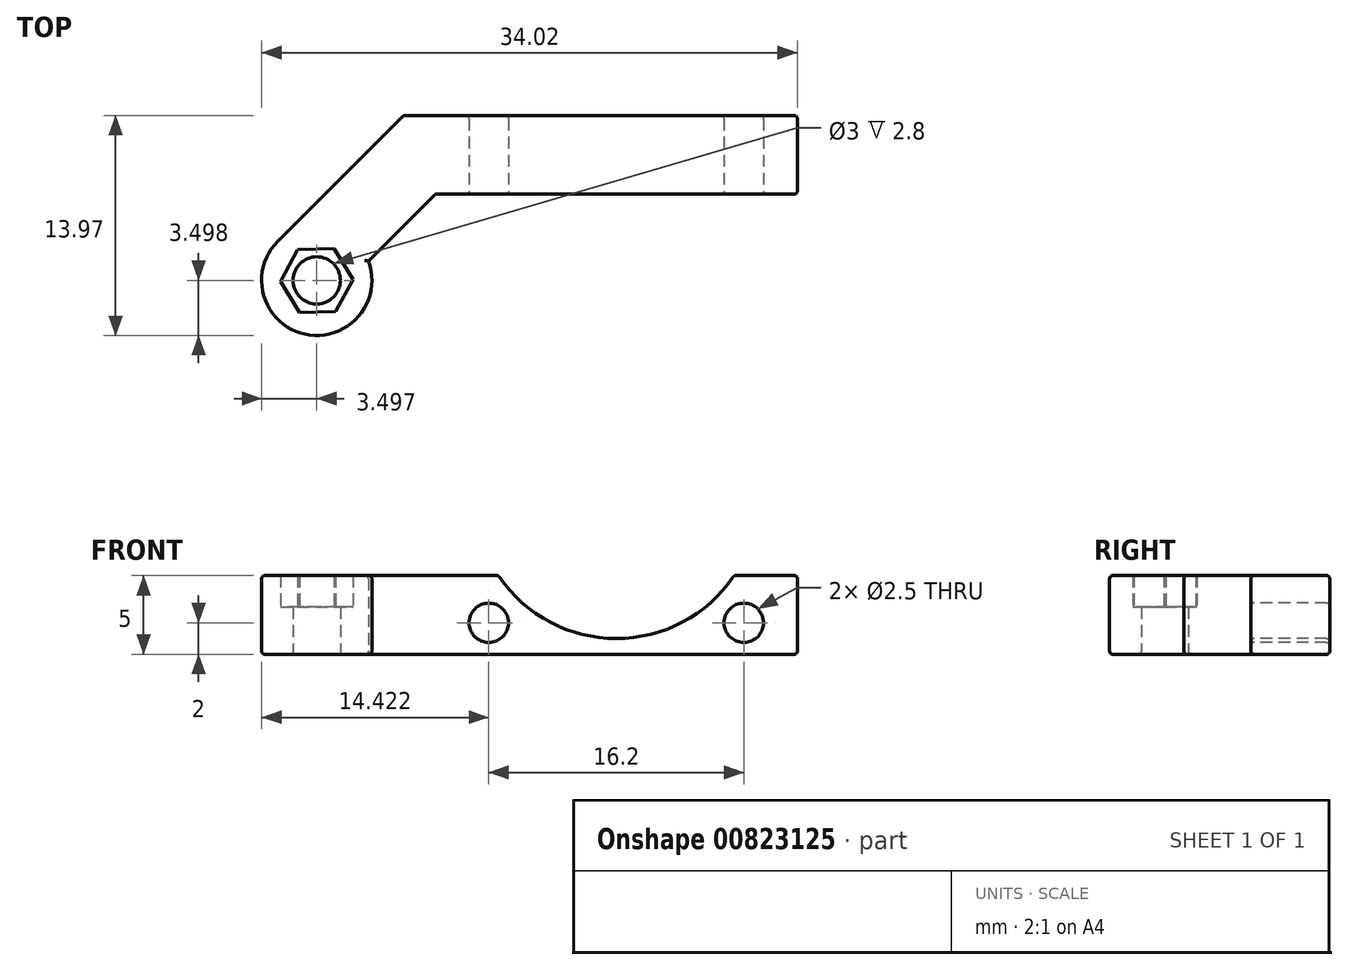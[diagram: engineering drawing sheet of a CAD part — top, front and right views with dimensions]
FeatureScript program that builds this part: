
annotation { "Feature Type Name" : "Feature", "Feature Type Description" : "" }
export const myFeature = defineFeature(function(context is Context, id is Id, definition is map)
    precondition{}
    {
        {
            var Q0;
            Q0=qCreatedBy(makeId("Top.planeOp"),FACE);
            var sketch = newSketch(context, id + "F0", { "sketchPlane" : qUnion([Q0])});
            skLineSegment(sketch, "E0", {"start": v(22.84, 7.04) * mm, "end": v(-2.16, 7.04) * mm});
            skLineSegment(sketch, "E1", {"start": v(-0.16, 2.04) * mm, "end": v(22.84, 2.04) * mm});
            skLineSegment(sketch, "E2", {"start": v(22.84, 2.04) * mm, "end": v(22.84, 7.04) * mm});
            skCircle(sketch, "E3", {"center": v(-7.68, -3.43) * mm, "radius": 1.5 * mm});
            skLineSegment(sketch, "E4", {"start": v(-7.68, 0) * mm, "end": v(-7.68, -6.73) * mm, "construction": true});
            skCircle(sketch, "E5", {"center": v(-7.68, -3.43) * mm, "radius": 3.5 * mm});
            skLineSegment(sketch, "E6", {"start": v(-2.16, 7.04) * mm, "end": v(-10.16, -0.96) * mm});
            skLineSegment(sketch, "E7", {"start": v(-4.4, -2.2) * mm, "end": v(-0.16, 2.04) * mm});
            skCircle(sketch, "E8.cCircle", {"center": v(-7.68, -3.43) * mm, "radius": 2 * mm, "construction": true});
            skLineSegment(sketch, "E8.0", {"start": v(-5.37, -3.37) * mm, "end": v(-6.47, -5.4) * mm});
            skLineSegment(sketch, "E8.1", {"start": v(-6.47, -5.4) * mm, "end": v(-8.78, -5.46) * mm});
            skLineSegment(sketch, "E8.2", {"start": v(-8.78, -5.46) * mm, "end": v(-10, -3.5) * mm});
            skLineSegment(sketch, "E8.3", {"start": v(-10, -3.5) * mm, "end": v(-8.9, -1.47) * mm});
            skLineSegment(sketch, "E8.4", {"start": v(-8.9, -1.47) * mm, "end": v(-6.59, -1.4) * mm});
            skLineSegment(sketch, "E8.5", {"start": v(-6.59, -1.4) * mm, "end": v(-5.37, -3.37) * mm});
            skPoint(sketch, "E8.0.midPoint", {"position": v(-5.92, -4.38) * mm});
            skSolve(sketch);
        }
        {
            var Q0;
            Q0 = qSketchRegion(id + "F0", true);
            var Q1;
            Q1=makeQuery(id+"F0.imprint","IMPRINT",FACE,{"disambiguationData":[TD([[makeQuery(id+"F0.imprint","IMPRINT",EDGE,{"derivedFrom":sQuery(id+"F0.wireOp",EDGE,"E3")}),-1.0]])]});
            extrude(context, id + "F1", {"entities" : qUnion([Q0, Q1]), "depth" : 5 * mm, "offsetDistance" : 25 * mm});
        }
        {
            var Q0;
            Q0=qCreatedBy(makeId("Front.planeOp"),FACE);
            var sketch = newSketch(context, id + "F2", { "sketchPlane" : qUnion([Q0])});
            skLineSegment(sketch, "E9", {"start": v(46.77, 2.5) * mm, "end": v(-32, 2.5) * mm, "construction": true});
            skLineSegment(sketch, "E10", {"start": v(11.34, 15) * mm, "end": v(11.34, 0) * mm, "construction": true});
            skCircle(sketch, "E11", {"center": v(3.24, 2) * mm, "radius": 1.25 * mm});
            skCircle(sketch, "E12", {"center": v(19.44, 2) * mm, "radius": 1.25 * mm});
            skCircle(sketch, "E13", {"center": v(11.34, 10) * mm, "radius": 9 * mm});
            skSolve(sketch);
        }
        {
            var Q0;
            Q0=makeQuery(id+"F2.imprint","IMPRINT",FACE,{"disambiguationData":[TD([[makeQuery(id+"F2.imprint","IMPRINT",EDGE,{"derivedFrom":sQuery(id+"F2.wireOp",EDGE,"E13")}),1.0]])]});
            var Q1;
            Q1=makeQuery(id+"F2.imprint","IMPRINT",FACE,{"disambiguationData":[TD([[makeQuery(id+"F2.imprint","IMPRINT",EDGE,{"derivedFrom":sQuery(id+"F2.wireOp",EDGE,"E12")}),1.0]])]});
            var Q2;
            Q2=makeQuery(id+"F2.imprint","IMPRINT",FACE,{"disambiguationData":[TD([[makeQuery(id+"F2.imprint","IMPRINT",EDGE,{"derivedFrom":sQuery(id+"F2.wireOp",EDGE,"E11")}),1.0]])]});
            var Q3;
            Q3=sQuery(id+"F2.wireOp",EDGE,"E13");
            var Q4;
            Q4=sQuery(id+"F2.wireOp",EDGE,"E12");
            var Q5;
            Q5=sQuery(id+"F2.wireOp",EDGE,"E11");
            extrude(context, id + "F3", {"entities" : qUnion([Q0, Q1, Q2]), "operationType" : NewBodyOperationType.REMOVE, "surfaceEntities" : qUnion([Q3, Q4, Q5]), "depth" : -15 * mm, "offsetDistance" : 25 * mm});
        }
        {
            var Q0;
            {var subQ0=sQuery(id+"F0.wireOp",EDGE,"E0");var subQ1=sQuery(id+"F0.wireOp",EDGE,"E2");Q0=makeQuery(id+"F3.boolean.opBoolean","SPLIT",EDGE,{"disambiguationData":[TD([makeQuery(id+"F1.opExtrude","SWEPT_FACE",FACE,{"disambiguationData":[OSD([subQ1])]})])],"derivedFrom":makeQuery(id+"F1.opExtrude","CAP_EDGE",EDGE,{"disambiguationData":[OSD([subQ0])],"isStart":false})});}
            var Q1;
            Q1=makeQuery(id+"F3.boolean.opBoolean","INTERSECT",EDGE,{"derivedFrom":[makeQuery(id+"F1.opExtrude","SWEPT_FACE",FACE,{"disambiguationData":[OSD([sQuery(id+"F0.wireOp",EDGE,"E0")])]}),makeQuery(id+"F3.opExtrude","SWEPT_FACE",FACE,{"disambiguationData":[OSD([sQuery(id+"F2.wireOp",EDGE,"E13")])]})]});
            var Q2;
            Q2=makeQuery(id+"F1.opExtrude","SWEPT_FACE",FACE,{"disambiguationData":[OSD([sQuery(id+"F0.wireOp",EDGE,"E1")])]});
            var Q3;
            Q3=makeQuery(id+"F1.opExtrude","SWEPT_FACE",FACE,{"disambiguationData":[OSD([sQuery(id+"F0.wireOp",EDGE,"E3")])]});
            var Q4;
            Q4=makeQuery(id+"F1.opExtrude","CAP_EDGE",EDGE,{"disambiguationData":[OSD([sQuery(id+"F0.wireOp",EDGE,"E2")])],"isStart":false});
            var Q5;
            Q5=makeQuery(id+"F1.opExtrude","CAP_EDGE",EDGE,{"disambiguationData":[OSD([sQuery(id+"F0.wireOp",EDGE,"0f24549b-c2e2-4721-b6e2-35617bd255be")])],"isStart":true});
            var Q6;
            Q6=makeQuery(id+"F1.opExtrude","SWEPT_EDGE",EDGE,{"disambiguationData":[OSD([sQuery(id+"F0.wireOp",EDGE,"Zt6ANnRh-k5cY-9Nom-YIyw-pIJQE4WEo30R"),sQuery(id+"F0.wireOp",EDGE,"0tKCsk9C-eRW9-mIZ1-Uz5l-tO1zgxtLd7ai")])]});
            var Q7;
            {var subQ0=sQuery(id+"F0.wireOp",EDGE,"E2");var subQ1=sQuery(id+"F0.wireOp",EDGE,"E1");Q7=makeQuery(id+"F3.boolean.opBoolean","SPLIT",EDGE,{"disambiguationData":[TD([makeQuery(id+"F1.opExtrude","SWEPT_FACE",FACE,{"disambiguationData":[OSD([subQ0])]})])],"derivedFrom":makeQuery(id+"F1.opExtrude","CAP_EDGE",EDGE,{"disambiguationData":[OSD([subQ1])],"isStart":false})});}
            var Q8;
            {var subQ0=sQuery(id+"F0.wireOp",EDGE,"E0");var subQ1=sQuery(id+"F0.wireOp",EDGE,"XOKBXjMK-aIrR-3Xav-z1c1-2tbnTsD4K69U");Q8=makeQuery(id+"F3.boolean.opBoolean","SPLIT",EDGE,{"disambiguationData":[TD([makeQuery(id+"F1.opExtrude","SWEPT_FACE",FACE,{"disambiguationData":[OSD([subQ1])]})])],"derivedFrom":makeQuery(id+"F1.opExtrude","CAP_EDGE",EDGE,{"disambiguationData":[OSD([subQ0])],"isStart":false})});}
            var Q9;
            Q9=makeQuery(id+"F3.boolean.opBoolean","INTERSECT",EDGE,{"disambiguationData":[OD(0.0)],"derivedFrom":[makeQuery(id+"F1.opExtrude","CAP_FACE",FACE,{"disambiguationData":[OSD([sQuery(id+"F0.wireOp",EDGE,"E0"),sQuery(id+"F0.wireOp",EDGE,"XOKBXjMK-aIrR-3Xav-z1c1-2tbnTsD4K69U"),sQuery(id+"F0.wireOp",EDGE,"5qDD20kP-8p41-NuGR-BYb0-utjdQ8Pf2vNB"),sQuery(id+"F0.wireOp",EDGE,"Zt6ANnRh-k5cY-9Nom-YIyw-pIJQE4WEo30R"),sQuery(id+"F0.wireOp",EDGE,"0tKCsk9C-eRW9-mIZ1-Uz5l-tO1zgxtLd7ai"),sQuery(id+"F0.wireOp",EDGE,"E1"),sQuery(id+"F0.wireOp",EDGE,"E2"),sQuery(id+"F0.wireOp",EDGE,"0f24549b-c2e2-4721-b6e2-35617bd255be"),sQuery(id+"F0.wireOp",EDGE,"E3")])],"isStart":false}),makeQuery(id+"F3.opExtrude","SWEPT_FACE",FACE,{"disambiguationData":[OSD([sQuery(id+"F2.wireOp",EDGE,"E13")])]})]});
            var Q10;
            {var subQ0=sQuery(id+"F0.wireOp",EDGE,"E1");var subQ1=sQuery(id+"F0.wireOp",EDGE,"0tKCsk9C-eRW9-mIZ1-Uz5l-tO1zgxtLd7ai");Q10=makeQuery(id+"F3.boolean.opBoolean","SPLIT",EDGE,{"disambiguationData":[TD([makeQuery(id+"F1.opExtrude","SWEPT_FACE",FACE,{"disambiguationData":[OSD([subQ1])]})])],"derivedFrom":makeQuery(id+"F1.opExtrude","CAP_EDGE",EDGE,{"disambiguationData":[OSD([subQ0])],"isStart":false})});}
            var Q11;
            Q11=makeQuery(id+"F1.opExtrude","CAP_EDGE",EDGE,{"disambiguationData":[OSD([sQuery(id+"F0.wireOp",EDGE,"Zt6ANnRh-k5cY-9Nom-YIyw-pIJQE4WEo30R")])],"isStart":false});
            var Q12;
            Q12=makeQuery(id+"F3.boolean.opBoolean","INTERSECT",EDGE,{"derivedFrom":[makeQuery(id+"F1.opExtrude","SWEPT_FACE",FACE,{"disambiguationData":[OSD([sQuery(id+"F0.wireOp",EDGE,"E1")])]}),makeQuery(id+"F3.opExtrude","SWEPT_FACE",FACE,{"disambiguationData":[OSD([sQuery(id+"F2.wireOp",EDGE,"E11")])]})]});
            var Q13;
            Q13=makeQuery(id+"F1.opExtrude","CAP_EDGE",EDGE,{"disambiguationData":[OSD([sQuery(id+"F0.wireOp",EDGE,"E2")])],"isStart":true});
            var Q14;
            Q14=makeQuery(id+"F1.opExtrude","CAP_FACE",FACE,{"disambiguationData":[OSD([sQuery(id+"F0.wireOp",EDGE,"E0"),sQuery(id+"F0.wireOp",EDGE,"XOKBXjMK-aIrR-3Xav-z1c1-2tbnTsD4K69U"),sQuery(id+"F0.wireOp",EDGE,"5qDD20kP-8p41-NuGR-BYb0-utjdQ8Pf2vNB"),sQuery(id+"F0.wireOp",EDGE,"Zt6ANnRh-k5cY-9Nom-YIyw-pIJQE4WEo30R"),sQuery(id+"F0.wireOp",EDGE,"0tKCsk9C-eRW9-mIZ1-Uz5l-tO1zgxtLd7ai"),sQuery(id+"F0.wireOp",EDGE,"E1"),sQuery(id+"F0.wireOp",EDGE,"E2"),sQuery(id+"F0.wireOp",EDGE,"0f24549b-c2e2-4721-b6e2-35617bd255be"),sQuery(id+"F0.wireOp",EDGE,"E3")])],"isStart":true});
            var Q15;
            Q15=makeQuery(id+"F1.opExtrude","CAP_EDGE",EDGE,{"disambiguationData":[OSD([sQuery(id+"F0.wireOp",EDGE,"XOKBXjMK-aIrR-3Xav-z1c1-2tbnTsD4K69U")])],"isStart":false});
            var Q16;
            Q16=makeQuery(id+"F1.opExtrude","CAP_EDGE",EDGE,{"disambiguationData":[OSD([sQuery(id+"F0.wireOp",EDGE,"0tKCsk9C-eRW9-mIZ1-Uz5l-tO1zgxtLd7ai")])],"isStart":false});
            var Q17;
            {var subQ0=sQuery(id+"F0.wireOp",EDGE,"5qDD20kP-8p41-NuGR-BYb0-utjdQ8Pf2vNB");var subQ1=sQuery(id+"F0.wireOp",EDGE,"XOKBXjMK-aIrR-3Xav-z1c1-2tbnTsD4K69U");var subQ2=sQuery(id+"F0.wireOp",EDGE,"Zt6ANnRh-k5cY-9Nom-YIyw-pIJQE4WEo30R");var subQ3=sQuery(id+"F0.wireOp",EDGE,"E0");var subQ4=sQuery(id+"F0.wireOp",EDGE,"0tKCsk9C-eRW9-mIZ1-Uz5l-tO1zgxtLd7ai");var subQ5=sQuery(id+"F0.wireOp",EDGE,"E1");var subQ6=sQuery(id+"F0.wireOp",EDGE,"0f24549b-c2e2-4721-b6e2-35617bd255be");var subQ7=sQuery(id+"F0.wireOp",EDGE,"E3");Q17=makeQuery(id+"F3.boolean.opBoolean","SPLIT",FACE,{"disambiguationData":[TD([makeQuery(id+"F1.opExtrude","SWEPT_FACE",FACE,{"disambiguationData":[OSD([subQ1])]})])],"derivedFrom":makeQuery(id+"F1.opExtrude","CAP_FACE",FACE,{"disambiguationData":[OSD([subQ3,subQ1,subQ0,subQ2,subQ4,subQ5,sQuery(id+"F0.wireOp",EDGE,"E2"),subQ6,subQ7])],"isStart":false})});}
            var Q18;
            Q18=makeQuery(id+"F1.opExtrude","SWEPT_EDGE",EDGE,{"disambiguationData":[OSD([sQuery(id+"F0.wireOp",EDGE,"E1"),sQuery(id+"F0.wireOp",EDGE,"E2")])]});
            var Q19;
            Q19=makeQuery(id+"F1.opExtrude","SWEPT_EDGE",EDGE,{"disambiguationData":[OSD([sQuery(id+"F0.wireOp",EDGE,"0tKCsk9C-eRW9-mIZ1-Uz5l-tO1zgxtLd7ai"),sQuery(id+"F0.wireOp",EDGE,"E1")])]});
            var Q20;
            Q20=makeQuery(id+"F1.opExtrude","CAP_EDGE",EDGE,{"disambiguationData":[OSD([sQuery(id+"F0.wireOp",EDGE,"E1")])],"isStart":true});
            var Q21;
            Q21=makeQuery(id+"F3.boolean.opBoolean","COPY",FACE,{"derivedFrom":makeQuery(id+"F3.opExtrude","SWEPT_FACE",FACE,{"disambiguationData":[OSD([sQuery(id+"F2.wireOp",EDGE,"E12")])]})});
            var Q22;
            Q22=makeQuery(id+"F1.opExtrude","CAP_EDGE",EDGE,{"disambiguationData":[OSD([sQuery(id+"F0.wireOp",EDGE,"Zt6ANnRh-k5cY-9Nom-YIyw-pIJQE4WEo30R")])],"isStart":true});
            var Q23;
            Q23=makeQuery(id+"F1.opExtrude","CAP_EDGE",EDGE,{"disambiguationData":[OSD([sQuery(id+"F0.wireOp",EDGE,"0f24549b-c2e2-4721-b6e2-35617bd255be")])],"isStart":false});
            var Q24;
            {var subQ0=sQuery(id+"F0.wireOp",EDGE,"E0");var subQ1=sQuery(id+"F0.wireOp",EDGE,"E1");var subQ2=sQuery(id+"F0.wireOp",EDGE,"E2");Q24=makeQuery(id+"F3.boolean.opBoolean","SPLIT",FACE,{"disambiguationData":[TD([makeQuery(id+"F1.opExtrude","SWEPT_FACE",FACE,{"disambiguationData":[OSD([subQ2])]})])],"derivedFrom":makeQuery(id+"F1.opExtrude","CAP_FACE",FACE,{"disambiguationData":[OSD([subQ0,sQuery(id+"F0.wireOp",EDGE,"XOKBXjMK-aIrR-3Xav-z1c1-2tbnTsD4K69U"),sQuery(id+"F0.wireOp",EDGE,"5qDD20kP-8p41-NuGR-BYb0-utjdQ8Pf2vNB"),sQuery(id+"F0.wireOp",EDGE,"Zt6ANnRh-k5cY-9Nom-YIyw-pIJQE4WEo30R"),sQuery(id+"F0.wireOp",EDGE,"0tKCsk9C-eRW9-mIZ1-Uz5l-tO1zgxtLd7ai"),subQ1,subQ2,sQuery(id+"F0.wireOp",EDGE,"0f24549b-c2e2-4721-b6e2-35617bd255be"),sQuery(id+"F0.wireOp",EDGE,"E3")])],"isStart":false})});}
            var Q25;
            Q25=makeQuery(id+"F1.opExtrude","SWEPT_FACE",FACE,{"disambiguationData":[OSD([sQuery(id+"F0.wireOp",EDGE,"XOKBXjMK-aIrR-3Xav-z1c1-2tbnTsD4K69U")])]});
            var Q26;
            Q26=makeQuery(id+"F1.opExtrude","CAP_EDGE",EDGE,{"disambiguationData":[OSD([sQuery(id+"F0.wireOp",EDGE,"0tKCsk9C-eRW9-mIZ1-Uz5l-tO1zgxtLd7ai")])],"isStart":true});
            var Q27;
            Q27=makeQuery(id+"F1.opExtrude","SWEPT_FACE",FACE,{"disambiguationData":[OSD([sQuery(id+"F0.wireOp",EDGE,"E2")])]});
            var Q28;
            Q28=makeQuery(id+"F1.opExtrude","SWEPT_FACE",FACE,{"disambiguationData":[OSD([sQuery(id+"F0.wireOp",EDGE,"5qDD20kP-8p41-NuGR-BYb0-utjdQ8Pf2vNB")])]});
            var Q29;
            Q29=makeQuery(id+"F3.boolean.opBoolean","COPY",FACE,{"derivedFrom":makeQuery(id+"F3.opExtrude","SWEPT_FACE",FACE,{"disambiguationData":[OSD([sQuery(id+"F2.wireOp",EDGE,"E13")])]})});
            var Q30;
            Q30=makeQuery(id+"F3.boolean.opBoolean","INTERSECT",EDGE,{"derivedFrom":[makeQuery(id+"F1.opExtrude","SWEPT_FACE",FACE,{"disambiguationData":[OSD([sQuery(id+"F0.wireOp",EDGE,"E1")])]}),makeQuery(id+"F3.opExtrude","SWEPT_FACE",FACE,{"disambiguationData":[OSD([sQuery(id+"F2.wireOp",EDGE,"E12")])]})]});
            var Q31;
            Q31=makeQuery(id+"F3.boolean.opBoolean","INTERSECT",EDGE,{"derivedFrom":[makeQuery(id+"F1.opExtrude","SWEPT_FACE",FACE,{"disambiguationData":[OSD([sQuery(id+"F0.wireOp",EDGE,"E1")])]}),makeQuery(id+"F3.opExtrude","SWEPT_FACE",FACE,{"disambiguationData":[OSD([sQuery(id+"F2.wireOp",EDGE,"E13")])]})]});
            var Q32;
            Q32=makeQuery(id+"F1.opExtrude","SWEPT_EDGE",EDGE,{"disambiguationData":[OSD([sQuery(id+"F0.wireOp",EDGE,"E0"),sQuery(id+"F0.wireOp",EDGE,"E2")])]});
            var Q33;
            Q33=makeQuery(id+"F1.opExtrude","SWEPT_EDGE",EDGE,{"disambiguationData":[OSD([sQuery(id+"F0.wireOp",EDGE,"l5DqmruQ-S4Sb-Dlvx-ZIcM-rorxe7HzB1pB"),sQuery(id+"F0.wireOp",EDGE,"Zt6ANnRh-k5cY-9Nom-YIyw-pIJQE4WEo30R"),sQuery(id+"F0.wireOp",EDGE,"0f24549b-c2e2-4721-b6e2-35617bd255be")])]});
            var Q34;
            Q34=makeQuery(id+"F1.opExtrude","SWEPT_FACE",FACE,{"disambiguationData":[OSD([sQuery(id+"F0.wireOp",EDGE,"E0")])]});
            var Q35;
            Q35=makeQuery(id+"F1.opExtrude","SWEPT_FACE",FACE,{"disambiguationData":[OSD([sQuery(id+"F0.wireOp",EDGE,"0tKCsk9C-eRW9-mIZ1-Uz5l-tO1zgxtLd7ai")])]});
            var Q36;
            Q36=makeQuery(id+"F1.opExtrude","CAP_EDGE",EDGE,{"disambiguationData":[OSD([sQuery(id+"F0.wireOp",EDGE,"5qDD20kP-8p41-NuGR-BYb0-utjdQ8Pf2vNB")])],"isStart":false});
            var Q37;
            Q37=makeQuery(id+"F3.boolean.opBoolean","COPY",FACE,{"derivedFrom":makeQuery(id+"F3.opExtrude","SWEPT_FACE",FACE,{"disambiguationData":[OSD([sQuery(id+"F2.wireOp",EDGE,"E11")])]})});
            var Q38;
            Q38=makeQuery(id+"F1.opExtrude","CAP_EDGE",EDGE,{"disambiguationData":[OSD([sQuery(id+"F0.wireOp",EDGE,"E3")])],"isStart":false});
            var Q39;
            Q39=makeQuery(id+"F3.boolean.opBoolean","INTERSECT",EDGE,{"disambiguationData":[OD(1.0)],"derivedFrom":[makeQuery(id+"F1.opExtrude","CAP_FACE",FACE,{"disambiguationData":[OSD([sQuery(id+"F0.wireOp",EDGE,"E0"),sQuery(id+"F0.wireOp",EDGE,"XOKBXjMK-aIrR-3Xav-z1c1-2tbnTsD4K69U"),sQuery(id+"F0.wireOp",EDGE,"5qDD20kP-8p41-NuGR-BYb0-utjdQ8Pf2vNB"),sQuery(id+"F0.wireOp",EDGE,"Zt6ANnRh-k5cY-9Nom-YIyw-pIJQE4WEo30R"),sQuery(id+"F0.wireOp",EDGE,"0tKCsk9C-eRW9-mIZ1-Uz5l-tO1zgxtLd7ai"),sQuery(id+"F0.wireOp",EDGE,"E1"),sQuery(id+"F0.wireOp",EDGE,"E2"),sQuery(id+"F0.wireOp",EDGE,"0f24549b-c2e2-4721-b6e2-35617bd255be"),sQuery(id+"F0.wireOp",EDGE,"E3")])],"isStart":false}),makeQuery(id+"F3.opExtrude","SWEPT_FACE",FACE,{"disambiguationData":[OSD([sQuery(id+"F2.wireOp",EDGE,"E13")])]})]});
            var Q40;
            Q40=makeQuery(id+"F1.opExtrude","SWEPT_FACE",FACE,{"disambiguationData":[OSD([sQuery(id+"F0.wireOp",EDGE,"Zt6ANnRh-k5cY-9Nom-YIyw-pIJQE4WEo30R")])]});
            var Q41;
            Q41=makeQuery(id+"F1.opExtrude","SWEPT_FACE",FACE,{"disambiguationData":[OSD([sQuery(id+"F0.wireOp",EDGE,"0f24549b-c2e2-4721-b6e2-35617bd255be")])]});
            var Q42;
            Q42=makeQuery(id+"F1.opExtrude","SWEPT_EDGE",EDGE,{"disambiguationData":[OSD([sQuery(id+"F0.wireOp",EDGE,"E0"),sQuery(id+"F0.wireOp",EDGE,"XOKBXjMK-aIrR-3Xav-z1c1-2tbnTsD4K69U")])]});
            var Q43;
            Q43=makeQuery(id+"F1.opExtrude","SWEPT_EDGE",EDGE,{"disambiguationData":[OSD([sQuery(id+"F0.wireOp",EDGE,"XOKBXjMK-aIrR-3Xav-z1c1-2tbnTsD4K69U"),sQuery(id+"F0.wireOp",EDGE,"5qDD20kP-8p41-NuGR-BYb0-utjdQ8Pf2vNB")])]});
            var Q44;
            Q44=makeQuery(id+"F1.opExtrude","CAP_EDGE",EDGE,{"disambiguationData":[OSD([sQuery(id+"F0.wireOp",EDGE,"E3")])],"isStart":true});
            var Q45;
            Q45=makeQuery(id+"F3.boolean.opBoolean","INTERSECT",EDGE,{"derivedFrom":[makeQuery(id+"F1.opExtrude","SWEPT_FACE",FACE,{"disambiguationData":[OSD([sQuery(id+"F0.wireOp",EDGE,"E0")])]}),makeQuery(id+"F3.opExtrude","SWEPT_FACE",FACE,{"disambiguationData":[OSD([sQuery(id+"F2.wireOp",EDGE,"E12")])]})]});
            var Q46;
            Q46=makeQuery(id+"F1.opExtrude","CAP_EDGE",EDGE,{"disambiguationData":[OSD([sQuery(id+"F0.wireOp",EDGE,"5qDD20kP-8p41-NuGR-BYb0-utjdQ8Pf2vNB")])],"isStart":true});
            var Q47;
            Q47=makeQuery(id+"F1.opExtrude","CAP_EDGE",EDGE,{"disambiguationData":[OSD([sQuery(id+"F0.wireOp",EDGE,"E0")])],"isStart":true});
            var Q48;
            Q48=makeQuery(id+"F1.opExtrude","SWEPT_EDGE",EDGE,{"disambiguationData":[OSD([sQuery(id+"F0.wireOp",EDGE,"5qDD20kP-8p41-NuGR-BYb0-utjdQ8Pf2vNB"),sQuery(id+"F0.wireOp",EDGE,"l5DqmruQ-S4Sb-Dlvx-ZIcM-rorxe7HzB1pB"),sQuery(id+"F0.wireOp",EDGE,"0f24549b-c2e2-4721-b6e2-35617bd255be")])]});
            var Q49;
            Q49=makeQuery(id+"F1.opExtrude","CAP_EDGE",EDGE,{"disambiguationData":[OSD([sQuery(id+"F0.wireOp",EDGE,"XOKBXjMK-aIrR-3Xav-z1c1-2tbnTsD4K69U")])],"isStart":true});
            var Q50;
            Q50=makeQuery(id+"F3.boolean.opBoolean","INTERSECT",EDGE,{"derivedFrom":[makeQuery(id+"F1.opExtrude","SWEPT_FACE",FACE,{"disambiguationData":[OSD([sQuery(id+"F0.wireOp",EDGE,"E0")])]}),makeQuery(id+"F3.opExtrude","SWEPT_FACE",FACE,{"disambiguationData":[OSD([sQuery(id+"F2.wireOp",EDGE,"E11")])]})]});
            var Q51;
            Q51=makeQuery(id+"F1.opExtrude","CAP_EDGE",EDGE,{"disambiguationData":[OSD([sQuery(id+"F0.wireOp",EDGE,"E5")])],"isStart":false});
            var Q52;
            Q52=makeQuery(id+"F1.opExtrude","CAP_EDGE",EDGE,{"disambiguationData":[OSD([sQuery(id+"F0.wireOp",EDGE,"E7")])],"isStart":false});
            fillet(context, id + "F4", {"entities" : qUnion([Q0, Q1, Q2, Q3, Q4, Q5, Q6, Q7, Q8, Q9, Q10, Q11, Q12, Q13, Q14, Q15, Q16, Q17, Q18, Q19, Q20, Q21, Q22, Q23, Q24, Q25, Q26, Q27, Q28, Q29, Q30, Q31, Q32, Q33, Q34, Q35, Q36, Q37, Q38, Q39, Q40, Q41, Q42, Q43, Q44, Q45, Q46, Q47, Q48, Q49, Q50, Q51, Q52]), "radius" : 0.2 * mm, "tangentPropagation" : true, "allowEdgeOverflow" : false});
        }
        {
            var Q0;
            Q0=makeQuery(id+"F0.imprint","IMPRINT",FACE,{"disambiguationData":[TD([[makeQuery(id+"F0.imprint","IMPRINT",EDGE,{"derivedFrom":sQuery(id+"F0.wireOp",EDGE,"E3")}),-1.0]])]});
            extrude(context, id + "F5", {"entities" : qUnion([Q0]), "operationType" : NewBodyOperationType.REMOVE, "depth" : 5 * mm, "offsetDistance" : 25 * mm, "hasSecondDirection" : true, "secondDirectionOppositeDirection" : false, "secondDirectionDepth" : 3 * mm});
        }
    });
